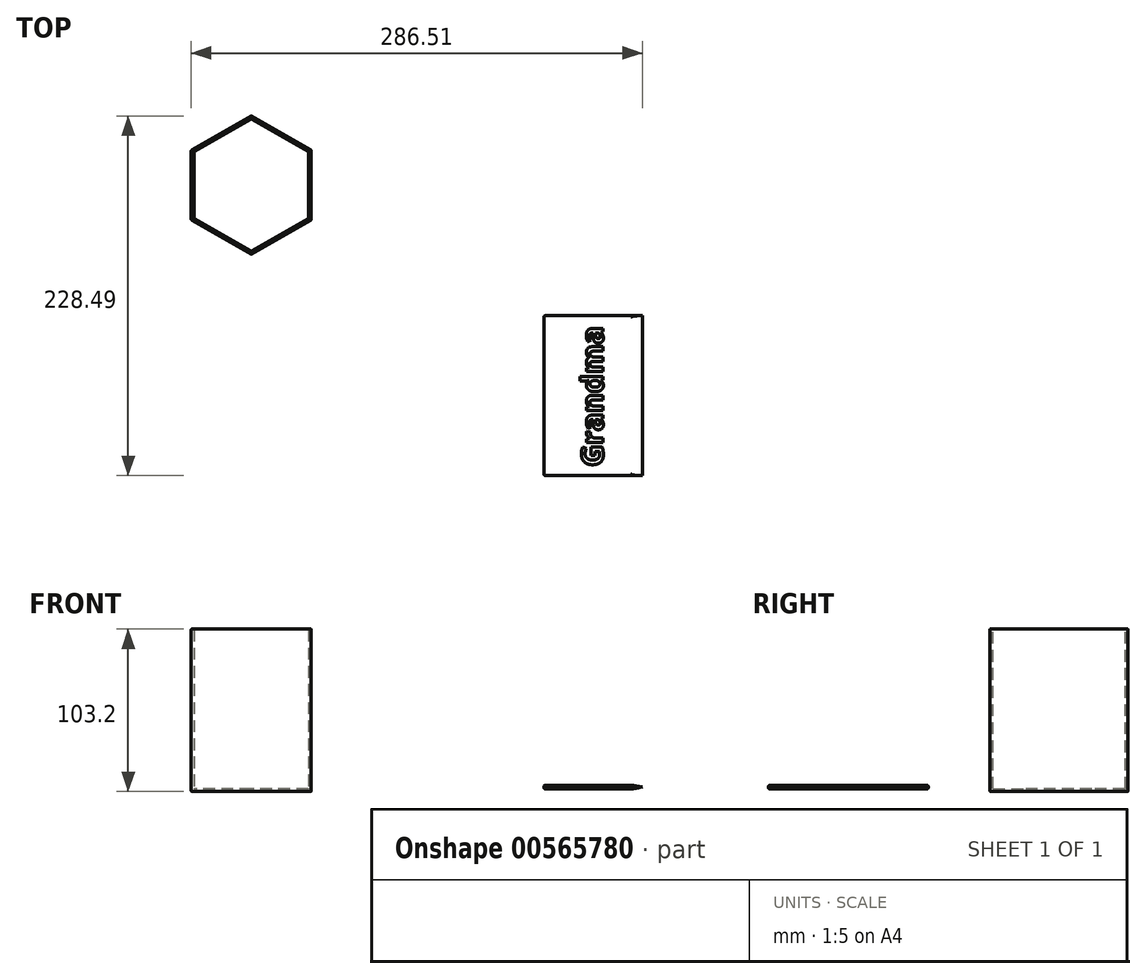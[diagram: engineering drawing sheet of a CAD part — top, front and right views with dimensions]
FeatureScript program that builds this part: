
annotation { "Feature Type Name" : "Feature", "Feature Type Description" : "" }
export const myFeature = defineFeature(function(context is Context, id is Id, definition is map)
    precondition{}
    {
        {
            var Q0;
            Q0=qCreatedBy(makeId("Top.planeOp"),FACE);
            var sketch = newSketch(context, id + "F0", { "sketchPlane" : qUnion([Q0])});
            skCircle(sketch, "E0.cCircle", {"center": v(0, 0) * mm, "radius": 38.1 * mm, "construction": true});
            skLineSegment(sketch, "E0.0", {"start": v(38.1, 22) * mm, "end": v(38.1, -22) * mm});
            skLineSegment(sketch, "E0.1", {"start": v(38.1, -22) * mm, "end": v(0, -44) * mm});
            skLineSegment(sketch, "E0.2", {"start": v(0, -44) * mm, "end": v(-38.1, -22) * mm});
            skLineSegment(sketch, "E0.3", {"start": v(-38.1, -22) * mm, "end": v(-38.1, 22) * mm});
            skLineSegment(sketch, "E0.4", {"start": v(-38.1, 22) * mm, "end": v(0, 44) * mm});
            skLineSegment(sketch, "E0.5", {"start": v(0, 44) * mm, "end": v(38.1, 22) * mm});
            skPoint(sketch, "E0.0.midPoint", {"position": v(38.1, 0) * mm});
            skLineSegment(sketch, "E1", {"start": v(-38.1, 0) * mm, "end": v(-36.5, 0) * mm});
            skCircle(sketch, "E2.cCircle", {"center": v(0, 0) * mm, "radius": 36.5 * mm, "construction": true});
            skLineSegment(sketch, "E2.0", {"start": v(-36.5, -21.07) * mm, "end": v(-36.5, 21.07) * mm});
            skLineSegment(sketch, "E2.1", {"start": v(-36.5, 21.07) * mm, "end": v(0, 42.15) * mm});
            skLineSegment(sketch, "E2.2", {"start": v(0, 42.15) * mm, "end": v(36.5, 21.07) * mm});
            skLineSegment(sketch, "E2.3", {"start": v(36.5, 21.07) * mm, "end": v(36.5, -21.07) * mm});
            skLineSegment(sketch, "E2.4", {"start": v(36.5, -21.07) * mm, "end": v(0, -42.15) * mm});
            skLineSegment(sketch, "E2.5", {"start": v(0, -42.15) * mm, "end": v(-36.5, -21.07) * mm});
            skPoint(sketch, "E2.0.midPoint", {"position": v(-36.5, 0) * mm});
            skSolve(sketch);
        }
        {
            var Q0;
            {var subQ0=sQuery(id+"F0.wireOp",EDGE,"E2.1");Q0=makeQuery(id+"F0.imprint","IMPRINT",FACE,{"disambiguationData":[TD([[makeQuery(id+"F0.imprint","IMPRINT",EDGE,{"derivedFrom":subQ0}),-1.0]])]});}
            var Q1;
            Q1=makeQuery(id+"F0.imprint","IMPRINT",FACE,{"disambiguationData":[TD([[makeQuery(id+"F0.imprint","IMPRINT",EDGE,{"derivedFrom":sQuery(id+"F0.wireOp",EDGE,"E0.0")}),-1.0]])]});
            extrude(context, id + "F1", {"entities" : qUnion([Q0, Q1]), "oppositeDirection" : true, "depth" : 1.6 * mm, "offsetDistance" : 25 * mm});
        }
        {
            var Q0;
            Q0=makeQuery(id+"F0.imprint","IMPRINT",FACE,{"disambiguationData":[TD([[makeQuery(id+"F0.imprint","IMPRINT",EDGE,{"derivedFrom":sQuery(id+"F0.wireOp",EDGE,"E0.0")}),-1.0]])]});
            extrude(context, id + "F2", {"entities" : qUnion([Q0]), "operationType" : NewBodyOperationType.ADD, "depth" : 101.6 * mm, "offsetDistance" : 25 * mm});
        }
        {
            var Q0;
            {var subQ0=sQuery(id+"F0.wireOp",EDGE,"E0.1");Q0=makeQuery(id+"F2.boolean.opBoolean","MERGE",FACE,{"derivedFrom":[makeQuery(id+"F1.opExtrude","SWEPT_FACE",FACE,{"disambiguationData":[OSD([subQ0])]}),makeQuery(id+"F2.opExtrude","SWEPT_FACE",FACE,{"disambiguationData":[OSD([subQ0])]})]});}
            var Q1;
            {var subQ0=sQuery(id+"F0.wireOp",EDGE,"E0.0");Q1=makeQuery(id+"F2.boolean.opBoolean","MERGE",FACE,{"derivedFrom":[makeQuery(id+"F1.opExtrude","SWEPT_FACE",FACE,{"disambiguationData":[OSD([subQ0])]}),makeQuery(id+"F2.opExtrude","SWEPT_FACE",FACE,{"disambiguationData":[OSD([subQ0])]})]});}
            var Q2;
            Q2=makeQuery(id+"F2.opExtrude","SWEPT_FACE",FACE,{"disambiguationData":[OSD([sQuery(id+"F0.wireOp",EDGE,"E2.0")])]});
            var Q3;
            Q3=makeQuery(id+"F2.opExtrude","SWEPT_FACE",FACE,{"disambiguationData":[OSD([sQuery(id+"F0.wireOp",EDGE,"E2.1")])]});
            var Q4;
            Q4=makeQuery(id+"F2.opExtrude","SWEPT_FACE",FACE,{"disambiguationData":[OSD([sQuery(id+"F0.wireOp",EDGE,"E2.2")])]});
            var Q5;
            {var subQ0=sQuery(id+"F0.wireOp",EDGE,"E0.5");Q5=makeQuery(id+"F2.boolean.opBoolean","MERGE",FACE,{"derivedFrom":[makeQuery(id+"F1.opExtrude","SWEPT_FACE",FACE,{"disambiguationData":[OSD([subQ0])]}),makeQuery(id+"F2.opExtrude","SWEPT_FACE",FACE,{"disambiguationData":[OSD([subQ0])]})]});}
            var Q6;
            {var subQ0=sQuery(id+"F0.wireOp",EDGE,"E0.4");Q6=makeQuery(id+"F2.boolean.opBoolean","MERGE",FACE,{"derivedFrom":[makeQuery(id+"F1.opExtrude","SWEPT_FACE",FACE,{"disambiguationData":[OSD([subQ0])]}),makeQuery(id+"F2.opExtrude","SWEPT_FACE",FACE,{"disambiguationData":[OSD([subQ0])]})]});}
            var Q7;
            {var subQ0=sQuery(id+"F0.wireOp",EDGE,"E0.3");Q7=makeQuery(id+"F2.boolean.opBoolean","MERGE",FACE,{"derivedFrom":[makeQuery(id+"F1.opExtrude","SWEPT_FACE",FACE,{"disambiguationData":[OSD([subQ0])]}),makeQuery(id+"F2.opExtrude","SWEPT_FACE",FACE,{"disambiguationData":[OSD([subQ0])]})]});}
            var Q8;
            {var subQ0=sQuery(id+"F0.wireOp",EDGE,"E0.2");Q8=makeQuery(id+"F2.boolean.opBoolean","MERGE",FACE,{"derivedFrom":[makeQuery(id+"F1.opExtrude","SWEPT_FACE",FACE,{"disambiguationData":[OSD([subQ0])]}),makeQuery(id+"F2.opExtrude","SWEPT_FACE",FACE,{"disambiguationData":[OSD([subQ0])]})]});}
            var Q9;
            Q9=makeQuery(id+"F2.opExtrude","SWEPT_FACE",FACE,{"disambiguationData":[OSD([sQuery(id+"F0.wireOp",EDGE,"E2.4")])]});
            var Q10;
            Q10=makeQuery(id+"F2.opExtrude","SWEPT_FACE",FACE,{"disambiguationData":[OSD([sQuery(id+"F0.wireOp",EDGE,"E2.5")])]});
            var Q11;
            Q11=makeQuery(id+"F2.opExtrude","SWEPT_FACE",FACE,{"disambiguationData":[OSD([sQuery(id+"F0.wireOp",EDGE,"E2.3")])]});
            var Q12;
            Q12=makeQuery(id+"F1.opExtrude","CAP_FACE",FACE,{"disambiguationData":[OSD([sQuery(id+"F0.wireOp",EDGE,"E0.0"),sQuery(id+"F0.wireOp",EDGE,"E0.1"),sQuery(id+"F0.wireOp",EDGE,"E0.2"),sQuery(id+"F0.wireOp",EDGE,"E0.3"),sQuery(id+"F0.wireOp",EDGE,"E0.4"),sQuery(id+"F0.wireOp",EDGE,"E0.5")])],"isStart":false});
            fillet(context, id + "F3", {"entities" : qUnion([Q0, Q1, Q2, Q3, Q4, Q5, Q6, Q7, Q8, Q9, Q10, Q11, Q12]), "radius" : .4 * mm, "tangentPropagation" : true, "allowEdgeOverflow" : false});
        }
        {
            var Q0;
            Q0=qCreatedBy(makeId("Top.planeOp"),FACE);
            var sketch = newSketch(context, id + "F4", { "sketchPlane" : qUnion([Q0])});
            skLineSegment(sketch, "E3.bottom", {"start": v(122.32, 18.64) * mm, "end": v(185.82, 18.64) * mm});
            skLineSegment(sketch, "E3.top", {"start": v(122.32, -82.96) * mm, "end": v(185.82, -82.96) * mm});
            skLineSegment(sketch, "E3.left", {"start": v(122.32, 18.64) * mm, "end": v(122.32, -82.96) * mm});
            skLineSegment(sketch, "E3.right", {"start": v(185.82, 18.64) * mm, "end": v(185.82, -82.96) * mm});
            skSolve(sketch);
        }
        {
            var Q0;
            Q0=makeQuery(id+"F4.imprint","IMPRINT",FACE,{"disambiguationData":[TD([[makeQuery(id+"F4.imprint","IMPRINT",EDGE,{"derivedFrom":sQuery(id+"F4.wireOp",EDGE,"E3.bottom")}),-1.0]])]});
            extrude(context, id + "F5", {"entities" : qUnion([Q0]), "depth" : 2.5 * mm, "offsetDistance" : 25 * mm});
        }
        {
            var Q0;
            Q0=makeQuery(id+"F5.opExtrude","CAP_EDGE",EDGE,{"disambiguationData":[OSD([sQuery(id+"F4.wireOp",EDGE,"E3.left")])],"isStart":false});
            var Q1;
            Q1=makeQuery(id+"F5.opExtrude","CAP_EDGE",EDGE,{"disambiguationData":[OSD([sQuery(id+"F4.wireOp",EDGE,"E3.left")])],"isStart":true});
            chamfer(context, id + "F6", {"entities" : qUnion([Q0, Q1]), "chamferType" : ChamferType.OFFSET_ANGLE, "width" : 8 * mm, "oppositeDirection" : false, "angle" : 10 * degree, "tangentPropagation" : true});
        }
        {
            var Q0;
            Q0=makeQuery(id+"F5.opExtrude","SWEPT_FACE",FACE,{"disambiguationData":[OSD([sQuery(id+"F4.wireOp",EDGE,"E3.top")])]});
            var sketch = newSketch(context, id + "F7", { "sketchPlane" : qUnion([Q0])});
            skLineSegment(sketch, "E4", {"start": v(185.82, 2.5) * mm, "end": v(185.82, 0) * mm});
            skLineSegment(sketch, "E5", {"start": v(185.82, 0) * mm, "end": v(185.82, 1.25) * mm});
            skCircle(sketch, "E6", {"center": v(185.82, 1.25) * mm, "radius": 5 * mm});
            skSolve(sketch);
        }
        {
            var Q0;
            Q0=makeQuery(id+"F5.opExtrude","SWEPT_FACE",FACE,{"disambiguationData":[OSD([sQuery(id+"F4.wireOp",EDGE,"E3.right")])]});
            var Q1;
            Q1=makeQuery(id+"F5.opExtrude","CAP_FACE",FACE,{"disambiguationData":[OSD([sQuery(id+"F4.wireOp",EDGE,"E3.bottom"),sQuery(id+"F4.wireOp",EDGE,"E3.top"),sQuery(id+"F4.wireOp",EDGE,"E3.left"),sQuery(id+"F4.wireOp",EDGE,"E3.right")])],"isStart":false});
            var Q2;
            Q2=makeQuery(id+"F5.opExtrude","CAP_FACE",FACE,{"disambiguationData":[OSD([sQuery(id+"F4.wireOp",EDGE,"E3.bottom"),sQuery(id+"F4.wireOp",EDGE,"E3.top"),sQuery(id+"F4.wireOp",EDGE,"E3.left"),sQuery(id+"F4.wireOp",EDGE,"E3.right")])],"isStart":true});
            fillet(context, id + "F8", {"entities" : qUnion([Q0, Q1, Q2]), "radius" : 1 * mm, "tangentPropagation" : true, "allowEdgeOverflow" : false});
        }
        {
            var Q0;
            Q0=makeQuery(id+"F5.opExtrude","SWEPT_BODY",BODY,{"disambiguationData":[OSD([sQuery(id+"F4.wireOp",EDGE,"E3.bottom"),sQuery(id+"F4.wireOp",EDGE,"E3.top"),sQuery(id+"F4.wireOp",EDGE,"E3.left"),sQuery(id+"F4.wireOp",EDGE,"E3.right")])]});
            var Q1;
            {var subQ0=sQuery(id+"F4.wireOp",EDGE,"E3.left");var subQ1=makeQuery(id+"F5.opExtrude","CAP_FACE",FACE,{"disambiguationData":[OSD([sQuery(id+"F4.wireOp",EDGE,"E3.bottom"),sQuery(id+"F4.wireOp",EDGE,"E3.top"),subQ0,sQuery(id+"F4.wireOp",EDGE,"E3.right")])],"isStart":false});Q1=makeQuery(id+"F8.opFillet","BLEND_EDGE",EDGE,{"blendedFrom":[makeQuery(id+"F6.opChamfer","BLEND_EDGE",EDGE,{"blendedFrom":[makeQuery(id+"F5.opExtrude","CAP_EDGE",EDGE,{"disambiguationData":[OSD([subQ0])],"isStart":false}),subQ1],"blendedInto":[subQ1]}),subQ1],"blendedInto":[subQ1]});}
            var Q2;
            Q2=sQuery(id+"F7.wireOp",EDGE,"E4");
            transform(context, id + "F9", {"entities" : qUnion([Q0]), "transformType" : TransformType.ROTATION, "transformAxis" : qUnion([Q2]), "angle" : 180 * degree, "oppositeDirection" : true, "makeCopy" : false});
        }
        {
            var Q0;
            Q0=makeQuery(id+"F5.opExtrude","CAP_FACE",FACE,{"disambiguationData":[OSD([sQuery(id+"F4.wireOp",EDGE,"E3.bottom"),sQuery(id+"F4.wireOp",EDGE,"E3.top"),sQuery(id+"F4.wireOp",EDGE,"E3.left"),sQuery(id+"F4.wireOp",EDGE,"E3.right")])],"isStart":false});
            var sketch = newSketch(context, id + "F10", { "sketchPlane" : qUnion([Q0])});
            skText(sketch, "E7", { "text": "Grandma", "fontName": "OpenSans-Bold.ttf"});
            skPoint(sketch, "E8.endSnap0", {"position": v(216.57, -178.78) * mm});
            const initialGuessF10  = {"E7": [0.22345, -0.17878, 0, 1, 0.01377]};
            skSetInitialGuess(sketch, initialGuessF10);
            skSolve(sketch);
        }
        {
            var Q0;
            Q0 = qSketchRegion(id + "F10", true);
            extrude(context, id + "F11", {"entities" : qUnion([Q0]), "operationType" : NewBodyOperationType.REMOVE, "oppositeDirection" : true, "depth" : 1 * mm, "offsetDistance" : 25 * mm});
        }
    });
